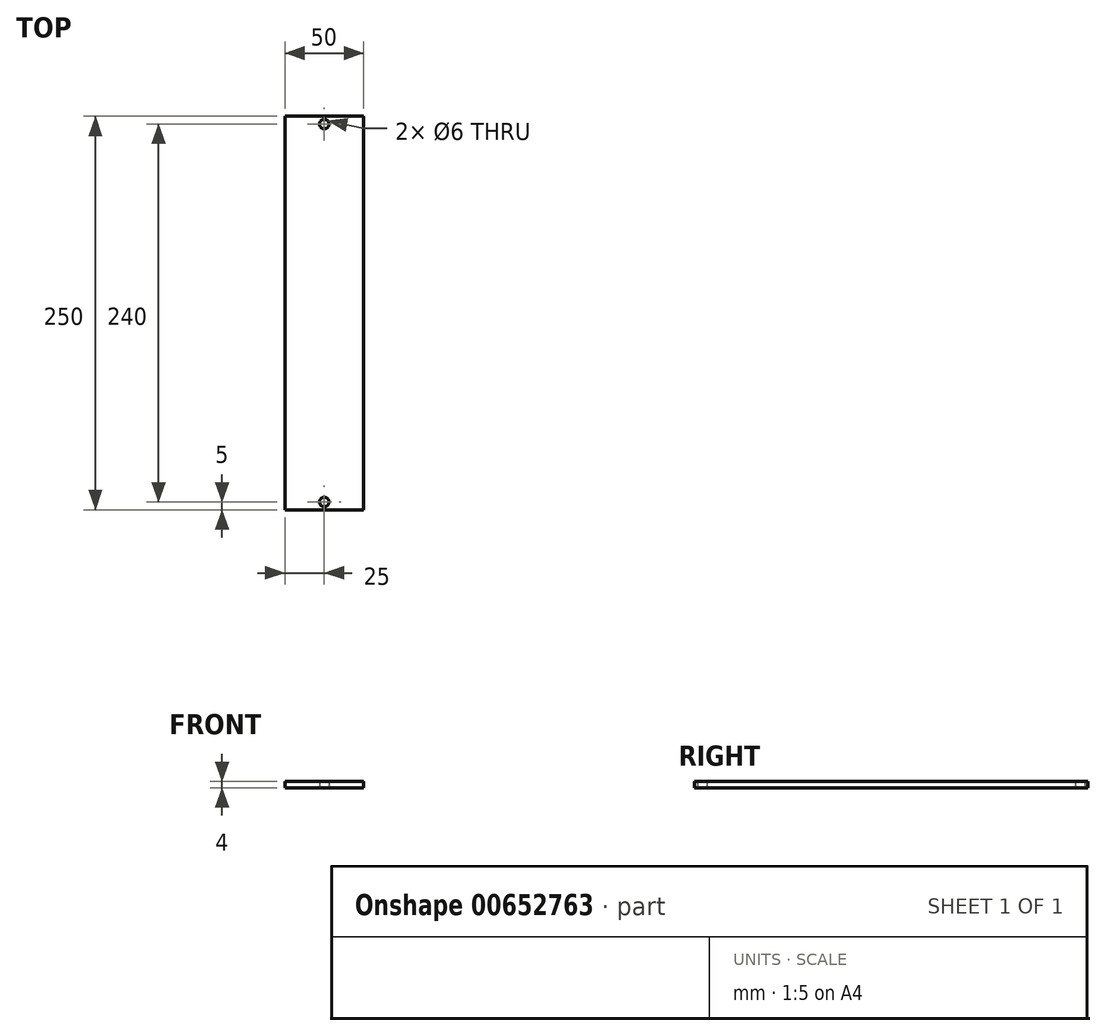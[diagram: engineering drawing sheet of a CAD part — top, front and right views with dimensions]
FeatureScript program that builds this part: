
annotation { "Feature Type Name" : "Feature", "Feature Type Description" : "" }
export const myFeature = defineFeature(function(context is Context, id is Id, definition is map)
    precondition{}
    {
        {
            var Q0;
            Q0=qCreatedBy(makeId("Top.planeOp"),FACE);
            var sketch = newSketch(context, id + "F0", { "sketchPlane" : qUnion([Q0])});
            skLineSegment(sketch, "E0.bottom", {"start": v(-25, 125) * mm, "end": v(25, 125) * mm});
            skLineSegment(sketch, "E0.top", {"start": v(-25, -125) * mm, "end": v(25, -125) * mm});
            skLineSegment(sketch, "E0.left", {"start": v(-25, 125) * mm, "end": v(-25, -125) * mm});
            skLineSegment(sketch, "E0.right", {"start": v(25, 125) * mm, "end": v(25, -125) * mm});
            skPoint(sketch, "E0.middle", {"position": v(0, 0) * mm});
            skCircle(sketch, "E1", {"center": v(0, 120) * mm, "radius": 3 * mm});
            skCircle(sketch, "E2", {"center": v(0, -120) * mm, "radius": 3 * mm});
            skLineSegment(sketch, "E3", {"start": v(0, 0) * mm, "end": v(0, 143.4) * mm, "construction": true});
            skLineSegment(sketch, "E4", {"start": v(0, 0) * mm, "end": v(0, -137.14) * mm});
            skSolve(sketch);
        }
        {
            var Q0;
            Q0=makeQuery(id+"F0.imprint","IMPRINT",FACE,{"disambiguationData":[TD([[makeQuery(id+"F0.imprint","IMPRINT",EDGE,{"derivedFrom":sQuery(id+"F0.wireOp",EDGE,"E0.bottom")}),-1.0]])]});
            extrude(context, id + "F1", {"entities" : qUnion([Q0]), "depth" : 4 * mm, "offsetDistance" : 25 * mm});
        }
    });
